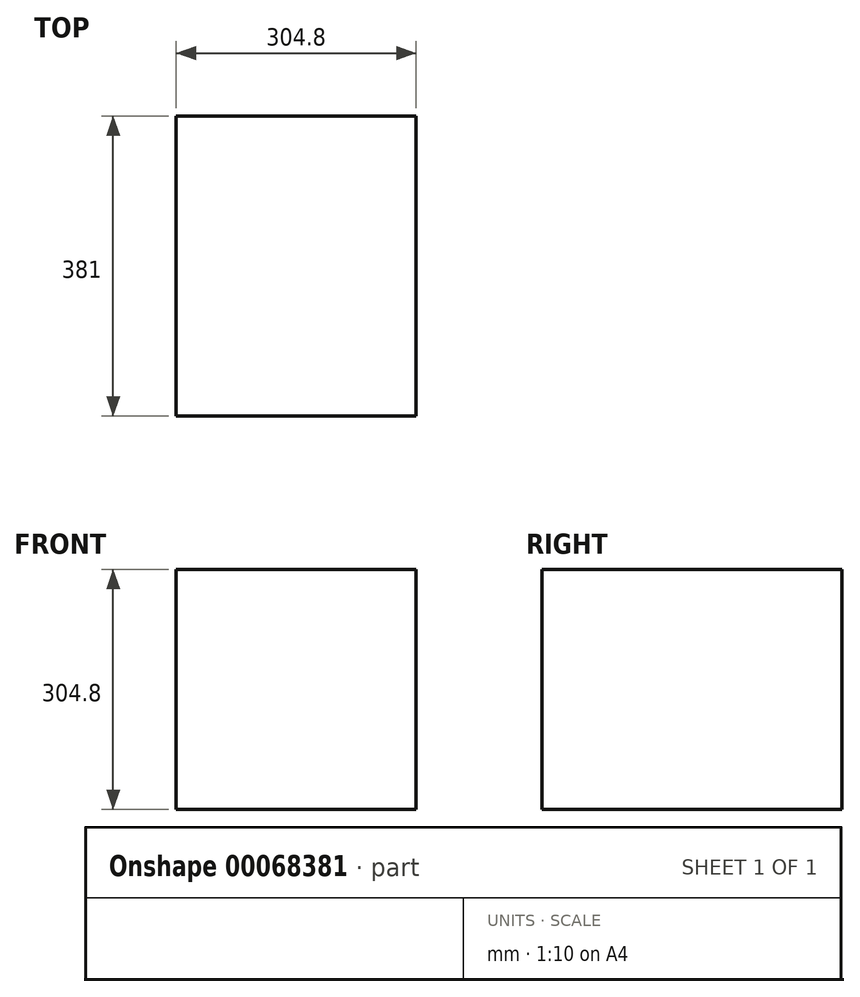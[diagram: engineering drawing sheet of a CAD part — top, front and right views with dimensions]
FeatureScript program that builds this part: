
annotation { "Feature Type Name" : "Feature", "Feature Type Description" : "" }
export const myFeature = defineFeature(function(context is Context, id is Id, definition is map)
    precondition{}
    {
        {
            var Q0;
            Q0=qCreatedBy(makeId("Front.planeOp"),FACE);
            var sketch = newSketch(context, id + "F0", { "sketchPlane" : qUnion([Q0])});
            skLineSegment(sketch, "E0.rect.bottom", {"start": v(152.4, 152.4) * mm, "end": v(-152.4, 152.4) * mm});
            skLineSegment(sketch, "E0.rect.top", {"start": v(152.4, -152.4) * mm, "end": v(-152.4, -152.4) * mm});
            skLineSegment(sketch, "E0.rect.left", {"start": v(152.4, 152.4) * mm, "end": v(152.4, -152.4) * mm});
            skLineSegment(sketch, "E0.rect.right", {"start": v(-152.4, 152.4) * mm, "end": v(-152.4, -152.4) * mm});
            skPoint(sketch, "E0.rect.middle", {"position": v(0, 0) * mm});
            skSolve(sketch);
        }
        {
            var Q0;
            Q0=makeQuery(id+"F0.imprint","IMPRINT",FACE,{"disambiguationData":[TD([[makeQuery(id+"F0.imprint","IMPRINT",EDGE,{"derivedFrom":sQuery(id+"F0.wireOp",EDGE,"E0.rect.bottom")}),1.0]])]});
            extrude(context, id + "F1", {"entities" : qUnion([Q0]), "depth" : 381 * mm});
        }
    });
